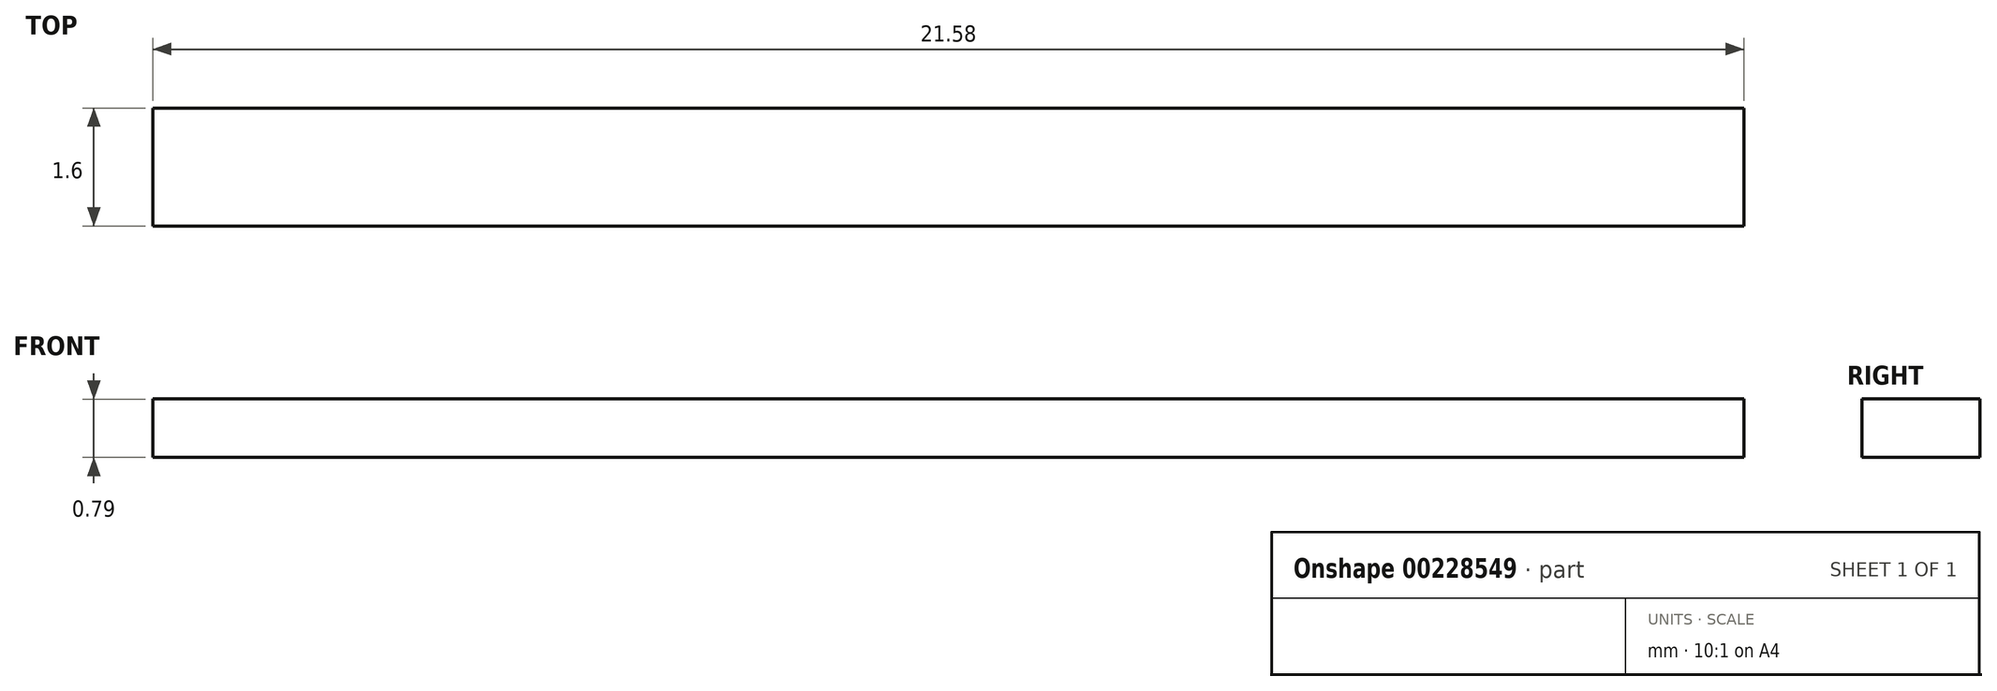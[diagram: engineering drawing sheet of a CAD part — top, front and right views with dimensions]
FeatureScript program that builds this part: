
annotation { "Feature Type Name" : "Feature", "Feature Type Description" : "" }
export const myFeature = defineFeature(function(context is Context, id is Id, definition is map)
    precondition{}
    {
        {
            var Q0;
            Q0=qCreatedBy(makeId("Top.planeOp"),FACE);
            var sketch = newSketch(context, id + "F0", { "sketchPlane" : qUnion([Q0])});
            skLineSegment(sketch, "E0.bottom", {"start": v(0, 0) * mm, "end": v(1879.6, 0) * mm});
            skLineSegment(sketch, "E0.top", {"start": v(0, -139.7) * mm, "end": v(1879.6, -139.7) * mm});
            skLineSegment(sketch, "E0.left", {"start": v(0, 0) * mm, "end": v(0, -139.7) * mm});
            skLineSegment(sketch, "E0.right", {"start": v(1879.6, 0) * mm, "end": v(1879.6, -139.7) * mm});
            skSolve(sketch);
        }
        {
            var Q0;
            Q0=makeQuery(id+"F0.imprint","IMPRINT",FACE,{"disambiguationData":[TD([[makeQuery(id+"F0.imprint","IMPRINT",EDGE,{"derivedFrom":sQuery(id+"F0.wireOp",EDGE,"E0.bottom")}),-1.0]])]});
            extrude(context, id + "F1", {"entities" : qUnion([Q0]), "depth" : 69.14 * mm});
        }
        {
            var Q0;
            Q0=makeQuery(id+"F1.opExtrude","SWEPT_BODY",BODY,{"disambiguationData":[OSD([sQuery(id+"F0.wireOp",EDGE,"E0.bottom"),sQuery(id+"F0.wireOp",EDGE,"E0.top"),sQuery(id+"F0.wireOp",EDGE,"E0.left"),sQuery(id+"F0.wireOp",EDGE,"E0.right")])]});
            var Q1;
            Q1=qCreatedBy(makeId("Origin.pointOp"),VERTEX);
            transform(context, id + "F2", {"entities" : qUnion([Q0]), "transformType" : TransformType.SCALE_UNIFORMLY, "scale" : 1 / 87.1, "scalePoint" : qUnion([Q1]), "makeCopy" : false});
        }
    });
